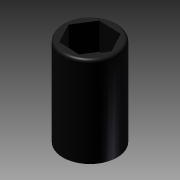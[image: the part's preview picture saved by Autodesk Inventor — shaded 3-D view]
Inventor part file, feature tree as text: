
AUTODESK INVENTOR PART (.ipt)
format: ipt  version: 2012 (Build 160160000, 160)  size: 91,136 bytes
history: native  units: mm
features: extrude x2, sketch x2, fillet x1
ambient origin geometry x8: Origin, YZ Plane, XZ Plane, XY Plane, X Axis, Y Axis, Z Axis, Center Point
bodies: Solid1 (feature_tree)
feature tree (5):
  extrude  "Extrusion1"  Depth=10.0mm TaperAngle=0.0deg
  extrude  "Extrusion2"  Depth=0.3mm
  fillet  "Fillet1"  [1 undecoded]
  sketch  "Sketch1"  dims[d0=6.0mm d1=10.0mm d2=0.0mm]
  sketch  "Sketch2"  dims[d3=3.0mm d4=0.0mm d5=0.3mm]
note: 1 required parameter value undecoded (feature->parameter linkage not recoverable at this tier; creation-order binding heuristic only, values carry confidence <= 0.55)
